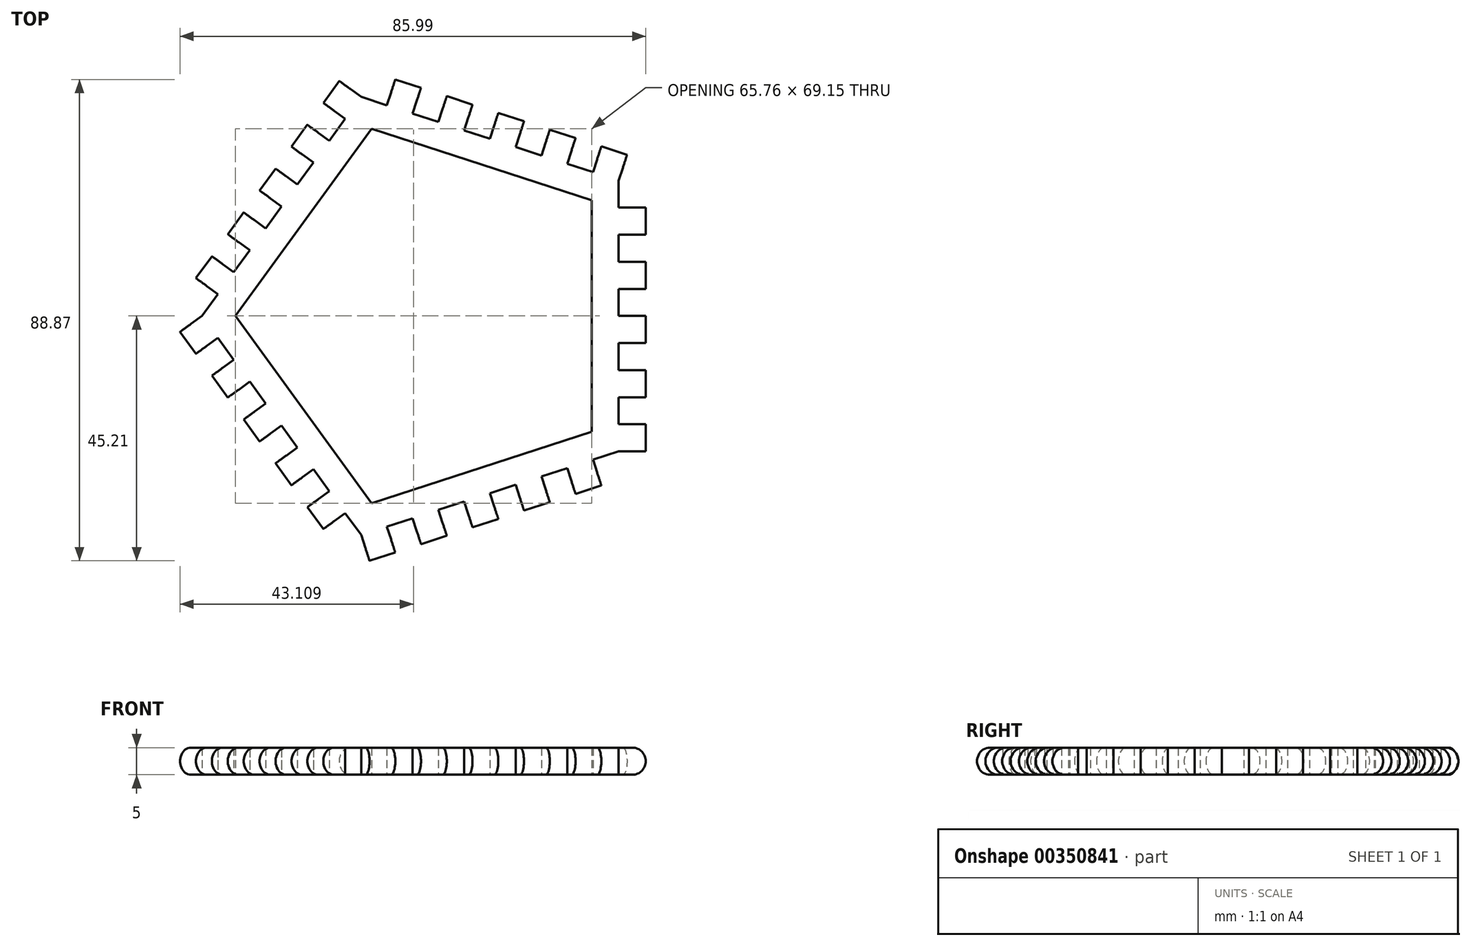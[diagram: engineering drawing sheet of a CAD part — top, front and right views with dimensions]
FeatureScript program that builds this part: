
annotation { "Feature Type Name" : "Feature", "Feature Type Description" : "" }
export const myFeature = defineFeature(function(context is Context, id is Id, definition is map)
    precondition{}
    {
        {
            var Q0;
            Q0=qCreatedBy(makeId("Top.planeOp"),FACE);
            var sketch = newSketch(context, id + "F0", { "sketchPlane" : qUnion([Q0])});
            skCircle(sketch, "E0.cCircle", {"center": v(0, 0) * mm, "radius": 34.4 * mm, "construction": true});
            skLineSegment(sketch, "E0.0", {"start": v(34.4, 25) * mm, "end": v(34.4, -25) * mm});
            skLineSegment(sketch, "E0.1", {"start": v(34.4, -25) * mm, "end": v(-13.14, -40.45) * mm});
            skLineSegment(sketch, "E0.2", {"start": v(-13.14, -40.45) * mm, "end": v(-42.53, 0) * mm});
            skLineSegment(sketch, "E0.3", {"start": v(-42.53, 0) * mm, "end": v(-13.14, 40.45) * mm});
            skLineSegment(sketch, "E0.4", {"start": v(-13.14, 40.45) * mm, "end": v(34.4, 25) * mm});
            skPoint(sketch, "E0.0.midPoint", {"position": v(34.4, 0) * mm});
            skLineSegment(sketch, "E1.bottom", {"start": v(34.4, -25) * mm, "end": v(39.4, -25) * mm});
            skLineSegment(sketch, "E1.top", {"start": v(34.4, -20) * mm, "end": v(39.4, -20) * mm});
            skLineSegment(sketch, "E1.left", {"start": v(34.4, -25) * mm, "end": v(34.4, -20) * mm});
            skLineSegment(sketch, "E1.right", {"start": v(39.4, -25) * mm, "end": v(39.4, -20) * mm});
            skLineSegment(sketch, "E2.0.1.0", {"start": v(34.4, -15) * mm, "end": v(34.4, -10) * mm});
            skLineSegment(sketch, "E2.0.1.1", {"start": v(34.4, -10) * mm, "end": v(39.4, -10) * mm});
            skLineSegment(sketch, "E2.0.1.2", {"start": v(39.4, -15) * mm, "end": v(39.4, -10) * mm});
            skLineSegment(sketch, "E2.0.1.3", {"start": v(34.4, -15) * mm, "end": v(39.4, -15) * mm});
            skLineSegment(sketch, "E2.0.2.0", {"start": v(34.4, -5) * mm, "end": v(34.4, 0) * mm});
            skLineSegment(sketch, "E2.0.2.1", {"start": v(34.4, 0) * mm, "end": v(39.4, 0) * mm});
            skLineSegment(sketch, "E2.0.2.2", {"start": v(39.4, -5) * mm, "end": v(39.4, 0) * mm});
            skLineSegment(sketch, "E2.0.2.3", {"start": v(34.4, -5) * mm, "end": v(39.4, -5) * mm});
            skLineSegment(sketch, "E2.0.3.0", {"start": v(34.4, 5) * mm, "end": v(34.4, 10) * mm});
            skLineSegment(sketch, "E2.0.3.1", {"start": v(34.4, 10) * mm, "end": v(39.4, 10) * mm});
            skLineSegment(sketch, "E2.0.3.2", {"start": v(39.4, 5) * mm, "end": v(39.4, 10) * mm});
            skLineSegment(sketch, "E2.0.3.3", {"start": v(34.4, 5) * mm, "end": v(39.4, 5) * mm});
            skLineSegment(sketch, "E2.0.4.0", {"start": v(34.4, 15) * mm, "end": v(34.4, 20) * mm});
            skLineSegment(sketch, "E2.0.4.1", {"start": v(34.4, 20) * mm, "end": v(39.4, 20) * mm});
            skLineSegment(sketch, "E2.0.4.2", {"start": v(39.4, 15) * mm, "end": v(39.4, 20) * mm});
            skLineSegment(sketch, "E2.0.4.3", {"start": v(34.4, 15) * mm, "end": v(39.4, 15) * mm});
            skLineSegment(sketch, "E2.direction2", {"start": v(34.4, -25) * mm, "end": v(34.4, -15) * mm, "construction": true});
            skLineSegment(sketch, "E3.1.0", {"start": v(29.65, 26.55) * mm, "end": v(31.2, 31.3) * mm});
            skLineSegment(sketch, "E3.1.1", {"start": v(35.95, 29.76) * mm, "end": v(31.2, 31.3) * mm});
            skLineSegment(sketch, "E3.1.2", {"start": v(34.4, 25) * mm, "end": v(35.95, 29.76) * mm});
            skLineSegment(sketch, "E3.1.3", {"start": v(20.14, 29.64) * mm, "end": v(21.69, 34.4) * mm});
            skLineSegment(sketch, "E3.1.4", {"start": v(26.44, 32.85) * mm, "end": v(21.69, 34.4) * mm});
            skLineSegment(sketch, "E3.1.5", {"start": v(24.9, 28.1) * mm, "end": v(26.44, 32.85) * mm});
            skLineSegment(sketch, "E3.1.6", {"start": v(10.63, 32.73) * mm, "end": v(12.18, 37.48) * mm});
            skLineSegment(sketch, "E3.1.7", {"start": v(16.93, 35.94) * mm, "end": v(12.18, 37.48) * mm});
            skLineSegment(sketch, "E3.1.8", {"start": v(15.39, 31.18) * mm, "end": v(16.93, 35.94) * mm});
            skLineSegment(sketch, "E3.1.9", {"start": v(1.12, 35.82) * mm, "end": v(2.67, 40.57) * mm});
            skLineSegment(sketch, "E3.1.10", {"start": v(7.42, 39.03) * mm, "end": v(2.67, 40.57) * mm});
            skLineSegment(sketch, "E3.1.11", {"start": v(5.88, 34.27) * mm, "end": v(7.42, 39.03) * mm});
            skLineSegment(sketch, "E3.1.12", {"start": v(-8.39, 38.9) * mm, "end": v(-6.84, 43.66) * mm});
            skLineSegment(sketch, "E3.1.13", {"start": v(-2.09, 42.12) * mm, "end": v(-6.84, 43.66) * mm});
            skLineSegment(sketch, "E3.1.14", {"start": v(-3.63, 37.36) * mm, "end": v(-2.09, 42.12) * mm});
            skLineSegment(sketch, "E3.2.0", {"start": v(-16.08, 36.4) * mm, "end": v(-20.13, 39.34) * mm});
            skLineSegment(sketch, "E3.2.1", {"start": v(-17.19, 43.39) * mm, "end": v(-20.13, 39.34) * mm});
            skLineSegment(sketch, "E3.2.2", {"start": v(-13.14, 40.45) * mm, "end": v(-17.19, 43.39) * mm});
            skLineSegment(sketch, "E3.2.3", {"start": v(-21.96, 28.32) * mm, "end": v(-26, 31.25) * mm});
            skLineSegment(sketch, "E3.2.4", {"start": v(-23.07, 35.3) * mm, "end": v(-26, 31.25) * mm});
            skLineSegment(sketch, "E3.2.5", {"start": v(-19.02, 32.36) * mm, "end": v(-23.07, 35.3) * mm});
            skLineSegment(sketch, "E3.2.6", {"start": v(-27.84, 20.23) * mm, "end": v(-31.88, 23.16) * mm});
            skLineSegment(sketch, "E3.2.7", {"start": v(-28.94, 27.2) * mm, "end": v(-31.88, 23.16) * mm});
            skLineSegment(sketch, "E3.2.8", {"start": v(-24.9, 24.27) * mm, "end": v(-28.94, 27.2) * mm});
            skLineSegment(sketch, "E3.2.9", {"start": v(-33.72, 12.14) * mm, "end": v(-37.76, 15.07) * mm});
            skLineSegment(sketch, "E3.2.10", {"start": v(-34.82, 19.12) * mm, "end": v(-37.76, 15.07) * mm});
            skLineSegment(sketch, "E3.2.11", {"start": v(-30.78, 16.18) * mm, "end": v(-34.82, 19.12) * mm});
            skLineSegment(sketch, "E3.2.12", {"start": v(-39.6, 4.05) * mm, "end": v(-43.64, 6.98) * mm});
            skLineSegment(sketch, "E3.2.13", {"start": v(-40.7, 11.03) * mm, "end": v(-43.64, 6.98) * mm});
            skLineSegment(sketch, "E3.2.14", {"start": v(-36.65, 8.1) * mm, "end": v(-40.7, 11.03) * mm});
            skLineSegment(sketch, "E3.3.0", {"start": v(-39.6, -4.05) * mm, "end": v(-43.64, -6.98) * mm});
            skLineSegment(sketch, "E3.3.1", {"start": v(-46.58, -2.94) * mm, "end": v(-43.64, -6.98) * mm});
            skLineSegment(sketch, "E3.3.2", {"start": v(-42.53, 0) * mm, "end": v(-46.58, -2.94) * mm});
            skLineSegment(sketch, "E3.3.3", {"start": v(-33.72, -12.14) * mm, "end": v(-37.76, -15.07) * mm});
            skLineSegment(sketch, "E3.3.4", {"start": v(-40.7, -11.03) * mm, "end": v(-37.76, -15.07) * mm});
            skLineSegment(sketch, "E3.3.5", {"start": v(-36.65, -8.1) * mm, "end": v(-40.7, -11.03) * mm});
            skLineSegment(sketch, "E3.3.6", {"start": v(-27.84, -20.23) * mm, "end": v(-31.88, -23.16) * mm});
            skLineSegment(sketch, "E3.3.7", {"start": v(-34.82, -19.12) * mm, "end": v(-31.88, -23.16) * mm});
            skLineSegment(sketch, "E3.3.8", {"start": v(-30.78, -16.18) * mm, "end": v(-34.82, -19.12) * mm});
            skLineSegment(sketch, "E3.3.9", {"start": v(-21.96, -28.32) * mm, "end": v(-26, -31.25) * mm});
            skLineSegment(sketch, "E3.3.10", {"start": v(-28.94, -27.2) * mm, "end": v(-26, -31.25) * mm});
            skLineSegment(sketch, "E3.3.11", {"start": v(-24.9, -24.27) * mm, "end": v(-28.94, -27.2) * mm});
            skLineSegment(sketch, "E3.3.12", {"start": v(-16.08, -36.4) * mm, "end": v(-20.13, -39.34) * mm});
            skLineSegment(sketch, "E3.3.13", {"start": v(-23.07, -35.3) * mm, "end": v(-20.13, -39.34) * mm});
            skLineSegment(sketch, "E3.3.14", {"start": v(-19.02, -32.36) * mm, "end": v(-23.07, -35.3) * mm});
            skLineSegment(sketch, "E3.4.0", {"start": v(-8.39, -38.9) * mm, "end": v(-6.84, -43.66) * mm});
            skLineSegment(sketch, "E3.4.1", {"start": v(-11.6, -45.2) * mm, "end": v(-6.84, -43.66) * mm});
            skLineSegment(sketch, "E3.4.2", {"start": v(-13.14, -40.45) * mm, "end": v(-11.6, -45.2) * mm});
            skLineSegment(sketch, "E3.4.3", {"start": v(1.12, -35.82) * mm, "end": v(2.67, -40.57) * mm});
            skLineSegment(sketch, "E3.4.4", {"start": v(-2.09, -42.12) * mm, "end": v(2.67, -40.57) * mm});
            skLineSegment(sketch, "E3.4.5", {"start": v(-3.63, -37.36) * mm, "end": v(-2.09, -42.12) * mm});
            skLineSegment(sketch, "E3.4.6", {"start": v(10.63, -32.73) * mm, "end": v(12.18, -37.48) * mm});
            skLineSegment(sketch, "E3.4.7", {"start": v(7.42, -39.03) * mm, "end": v(12.18, -37.48) * mm});
            skLineSegment(sketch, "E3.4.8", {"start": v(5.88, -34.27) * mm, "end": v(7.42, -39.03) * mm});
            skLineSegment(sketch, "E3.4.9", {"start": v(20.14, -29.64) * mm, "end": v(21.69, -34.4) * mm});
            skLineSegment(sketch, "E3.4.10", {"start": v(16.93, -35.94) * mm, "end": v(21.69, -34.4) * mm});
            skLineSegment(sketch, "E3.4.11", {"start": v(15.39, -31.18) * mm, "end": v(16.93, -35.94) * mm});
            skLineSegment(sketch, "E3.4.12", {"start": v(29.65, -26.55) * mm, "end": v(31.2, -31.3) * mm});
            skLineSegment(sketch, "E3.4.13", {"start": v(26.44, -32.85) * mm, "end": v(31.2, -31.3) * mm});
            skLineSegment(sketch, "E3.4.14", {"start": v(24.9, -28.1) * mm, "end": v(26.44, -32.85) * mm});
            skLineSegment(sketch, "E4.0", {"start": v(29.4, 21.37) * mm, "end": v(29.4, -21.37) * mm});
            skLineSegment(sketch, "E4.1", {"start": v(-11.23, 34.57) * mm, "end": v(29.4, 21.37) * mm});
            skLineSegment(sketch, "E4.2", {"start": v(29.4, -21.37) * mm, "end": v(-11.23, -34.57) * mm});
            skLineSegment(sketch, "E4.3", {"start": v(-11.23, -34.57) * mm, "end": v(-36.35, 0) * mm});
            skLineSegment(sketch, "E4.4", {"start": v(-36.35, 0) * mm, "end": v(-11.23, 34.57) * mm});
            skSolve(sketch);
        }
        {
            var Q0;
            Q0 = qSketchRegion(id + "F0", true);
            extrude(context, id + "F1", {"entities" : qUnion([Q0]), "depth" : 5 * mm});
        }
        {
            var Q0;
            Q0=makeQuery(id+"F1.opExtrude","CAP_EDGE",EDGE,{"disambiguationData":[OSD([sQuery(id+"F0.wireOp",EDGE,"E3.2.1")])],"isStart":false});
            var Q1;
            Q1=makeQuery(id+"F1.opExtrude","CAP_EDGE",EDGE,{"disambiguationData":[OSD([sQuery(id+"F0.wireOp",EDGE,"E3.2.4")])],"isStart":false});
            var Q2;
            Q2=makeQuery(id+"F1.opExtrude","CAP_EDGE",EDGE,{"disambiguationData":[OSD([sQuery(id+"F0.wireOp",EDGE,"E3.2.7")])],"isStart":false});
            var Q3;
            Q3=makeQuery(id+"F1.opExtrude","CAP_EDGE",EDGE,{"disambiguationData":[OSD([sQuery(id+"F0.wireOp",EDGE,"E3.2.10")])],"isStart":false});
            var Q4;
            Q4=makeQuery(id+"F1.opExtrude","CAP_EDGE",EDGE,{"disambiguationData":[OSD([sQuery(id+"F0.wireOp",EDGE,"E3.2.13")])],"isStart":false});
            var Q5;
            Q5=makeQuery(id+"F1.opExtrude","CAP_EDGE",EDGE,{"disambiguationData":[OSD([sQuery(id+"F0.wireOp",EDGE,"E3.3.1")])],"isStart":false});
            var Q6;
            Q6=makeQuery(id+"F1.opExtrude","CAP_EDGE",EDGE,{"disambiguationData":[OSD([sQuery(id+"F0.wireOp",EDGE,"E3.3.4")])],"isStart":false});
            var Q7;
            Q7=makeQuery(id+"F1.opExtrude","CAP_EDGE",EDGE,{"disambiguationData":[OSD([sQuery(id+"F0.wireOp",EDGE,"E3.3.7")])],"isStart":false});
            var Q8;
            Q8=makeQuery(id+"F1.opExtrude","CAP_EDGE",EDGE,{"disambiguationData":[OSD([sQuery(id+"F0.wireOp",EDGE,"E3.3.10")])],"isStart":false});
            var Q9;
            Q9=makeQuery(id+"F1.opExtrude","CAP_EDGE",EDGE,{"disambiguationData":[OSD([sQuery(id+"F0.wireOp",EDGE,"E3.3.13")])],"isStart":false});
            var Q10;
            Q10=makeQuery(id+"F1.opExtrude","CAP_EDGE",EDGE,{"disambiguationData":[OSD([sQuery(id+"F0.wireOp",EDGE,"E3.4.1")])],"isStart":false});
            var Q11;
            Q11=makeQuery(id+"F1.opExtrude","CAP_EDGE",EDGE,{"disambiguationData":[OSD([sQuery(id+"F0.wireOp",EDGE,"E3.4.4")])],"isStart":false});
            var Q12;
            Q12=makeQuery(id+"F1.opExtrude","CAP_EDGE",EDGE,{"disambiguationData":[OSD([sQuery(id+"F0.wireOp",EDGE,"E3.4.7")])],"isStart":false});
            var Q13;
            Q13=makeQuery(id+"F1.opExtrude","CAP_EDGE",EDGE,{"disambiguationData":[OSD([sQuery(id+"F0.wireOp",EDGE,"E3.4.10")])],"isStart":false});
            var Q14;
            Q14=makeQuery(id+"F1.opExtrude","CAP_EDGE",EDGE,{"disambiguationData":[OSD([sQuery(id+"F0.wireOp",EDGE,"E3.4.13")])],"isStart":false});
            var Q15;
            Q15=makeQuery(id+"F1.opExtrude","CAP_EDGE",EDGE,{"disambiguationData":[OSD([sQuery(id+"F0.wireOp",EDGE,"E1.right")])],"isStart":false});
            var Q16;
            Q16=makeQuery(id+"F1.opExtrude","CAP_EDGE",EDGE,{"disambiguationData":[OSD([sQuery(id+"F0.wireOp",EDGE,"E2.0.1.2")])],"isStart":false});
            var Q17;
            Q17=makeQuery(id+"F1.opExtrude","CAP_EDGE",EDGE,{"disambiguationData":[OSD([sQuery(id+"F0.wireOp",EDGE,"E2.0.2.2")])],"isStart":false});
            var Q18;
            Q18=makeQuery(id+"F1.opExtrude","CAP_EDGE",EDGE,{"disambiguationData":[OSD([sQuery(id+"F0.wireOp",EDGE,"E2.0.3.2")])],"isStart":false});
            var Q19;
            Q19=makeQuery(id+"F1.opExtrude","CAP_EDGE",EDGE,{"disambiguationData":[OSD([sQuery(id+"F0.wireOp",EDGE,"E2.0.4.2")])],"isStart":false});
            var Q20;
            Q20=makeQuery(id+"F1.opExtrude","CAP_EDGE",EDGE,{"disambiguationData":[OSD([sQuery(id+"F0.wireOp",EDGE,"E3.1.1")])],"isStart":false});
            var Q21;
            Q21=makeQuery(id+"F1.opExtrude","CAP_EDGE",EDGE,{"disambiguationData":[OSD([sQuery(id+"F0.wireOp",EDGE,"E3.1.4")])],"isStart":false});
            var Q22;
            Q22=makeQuery(id+"F1.opExtrude","CAP_EDGE",EDGE,{"disambiguationData":[OSD([sQuery(id+"F0.wireOp",EDGE,"E3.1.7")])],"isStart":false});
            var Q23;
            Q23=makeQuery(id+"F1.opExtrude","CAP_EDGE",EDGE,{"disambiguationData":[OSD([sQuery(id+"F0.wireOp",EDGE,"E3.1.10")])],"isStart":false});
            var Q24;
            Q24=makeQuery(id+"F1.opExtrude","CAP_EDGE",EDGE,{"disambiguationData":[OSD([sQuery(id+"F0.wireOp",EDGE,"E3.1.13")])],"isStart":false});
            var Q25;
            Q25=makeQuery(id+"F1.opExtrude","CAP_EDGE",EDGE,{"disambiguationData":[OSD([sQuery(id+"F0.wireOp",EDGE,"E3.4.1")])],"isStart":true});
            var Q26;
            Q26=makeQuery(id+"F1.opExtrude","CAP_EDGE",EDGE,{"disambiguationData":[OSD([sQuery(id+"F0.wireOp",EDGE,"E3.4.4")])],"isStart":true});
            var Q27;
            Q27=makeQuery(id+"F1.opExtrude","CAP_EDGE",EDGE,{"disambiguationData":[OSD([sQuery(id+"F0.wireOp",EDGE,"E3.4.7")])],"isStart":true});
            var Q28;
            Q28=makeQuery(id+"F1.opExtrude","CAP_EDGE",EDGE,{"disambiguationData":[OSD([sQuery(id+"F0.wireOp",EDGE,"E3.4.10")])],"isStart":true});
            var Q29;
            Q29=makeQuery(id+"F1.opExtrude","CAP_EDGE",EDGE,{"disambiguationData":[OSD([sQuery(id+"F0.wireOp",EDGE,"E3.4.13")])],"isStart":true});
            var Q30;
            Q30=makeQuery(id+"F1.opExtrude","CAP_EDGE",EDGE,{"disambiguationData":[OSD([sQuery(id+"F0.wireOp",EDGE,"E1.right")])],"isStart":true});
            var Q31;
            Q31=makeQuery(id+"F1.opExtrude","CAP_EDGE",EDGE,{"disambiguationData":[OSD([sQuery(id+"F0.wireOp",EDGE,"E2.0.1.2")])],"isStart":true});
            var Q32;
            Q32=makeQuery(id+"F1.opExtrude","CAP_EDGE",EDGE,{"disambiguationData":[OSD([sQuery(id+"F0.wireOp",EDGE,"E2.0.2.2")])],"isStart":true});
            var Q33;
            Q33=makeQuery(id+"F1.opExtrude","CAP_EDGE",EDGE,{"disambiguationData":[OSD([sQuery(id+"F0.wireOp",EDGE,"E2.0.3.2")])],"isStart":true});
            var Q34;
            Q34=makeQuery(id+"F1.opExtrude","CAP_EDGE",EDGE,{"disambiguationData":[OSD([sQuery(id+"F0.wireOp",EDGE,"E2.0.4.2")])],"isStart":true});
            var Q35;
            Q35=makeQuery(id+"F1.opExtrude","CAP_EDGE",EDGE,{"disambiguationData":[OSD([sQuery(id+"F0.wireOp",EDGE,"E3.1.1")])],"isStart":true});
            var Q36;
            Q36=makeQuery(id+"F1.opExtrude","CAP_EDGE",EDGE,{"disambiguationData":[OSD([sQuery(id+"F0.wireOp",EDGE,"E3.1.4")])],"isStart":true});
            var Q37;
            Q37=makeQuery(id+"F1.opExtrude","CAP_EDGE",EDGE,{"disambiguationData":[OSD([sQuery(id+"F0.wireOp",EDGE,"E3.1.7")])],"isStart":true});
            var Q38;
            Q38=makeQuery(id+"F1.opExtrude","CAP_EDGE",EDGE,{"disambiguationData":[OSD([sQuery(id+"F0.wireOp",EDGE,"E3.1.10")])],"isStart":true});
            var Q39;
            Q39=makeQuery(id+"F1.opExtrude","CAP_EDGE",EDGE,{"disambiguationData":[OSD([sQuery(id+"F0.wireOp",EDGE,"E3.1.13")])],"isStart":true});
            var Q40;
            Q40=makeQuery(id+"F1.opExtrude","CAP_EDGE",EDGE,{"disambiguationData":[OSD([sQuery(id+"F0.wireOp",EDGE,"E3.2.1")])],"isStart":true});
            var Q41;
            Q41=makeQuery(id+"F1.opExtrude","CAP_EDGE",EDGE,{"disambiguationData":[OSD([sQuery(id+"F0.wireOp",EDGE,"E3.2.4")])],"isStart":true});
            var Q42;
            Q42=makeQuery(id+"F1.opExtrude","CAP_EDGE",EDGE,{"disambiguationData":[OSD([sQuery(id+"F0.wireOp",EDGE,"E3.2.7")])],"isStart":true});
            var Q43;
            Q43=makeQuery(id+"F1.opExtrude","CAP_EDGE",EDGE,{"disambiguationData":[OSD([sQuery(id+"F0.wireOp",EDGE,"E3.2.10")])],"isStart":true});
            var Q44;
            Q44=makeQuery(id+"F1.opExtrude","CAP_EDGE",EDGE,{"disambiguationData":[OSD([sQuery(id+"F0.wireOp",EDGE,"E3.2.13")])],"isStart":true});
            var Q45;
            Q45=makeQuery(id+"F1.opExtrude","CAP_EDGE",EDGE,{"disambiguationData":[OSD([sQuery(id+"F0.wireOp",EDGE,"E3.3.1")])],"isStart":true});
            var Q46;
            Q46=makeQuery(id+"F1.opExtrude","CAP_EDGE",EDGE,{"disambiguationData":[OSD([sQuery(id+"F0.wireOp",EDGE,"E3.3.4")])],"isStart":true});
            var Q47;
            Q47=makeQuery(id+"F1.opExtrude","CAP_EDGE",EDGE,{"disambiguationData":[OSD([sQuery(id+"F0.wireOp",EDGE,"E3.3.7")])],"isStart":true});
            var Q48;
            Q48=makeQuery(id+"F1.opExtrude","CAP_EDGE",EDGE,{"disambiguationData":[OSD([sQuery(id+"F0.wireOp",EDGE,"E3.3.10")])],"isStart":true});
            var Q49;
            Q49=makeQuery(id+"F1.opExtrude","CAP_EDGE",EDGE,{"disambiguationData":[OSD([sQuery(id+"F0.wireOp",EDGE,"E3.3.13")])],"isStart":true});
            fillet(context, id + "F2", {"entities" : qUnion([Q0, Q1, Q2, Q3, Q4, Q5, Q6, Q7, Q8, Q9, Q10, Q11, Q12, Q13, Q14, Q15, Q16, Q17, Q18, Q19, Q20, Q21, Q22, Q23, Q24, Q25, Q26, Q27, Q28, Q29, Q30, Q31, Q32, Q33, Q34, Q35, Q36, Q37, Q38, Q39, Q40, Q41, Q42, Q43, Q44, Q45, Q46, Q47, Q48, Q49]), "radius" : 2.5 * mm, "tangentPropagation" : true, "allowEdgeOverflow" : false});
        }
    });
